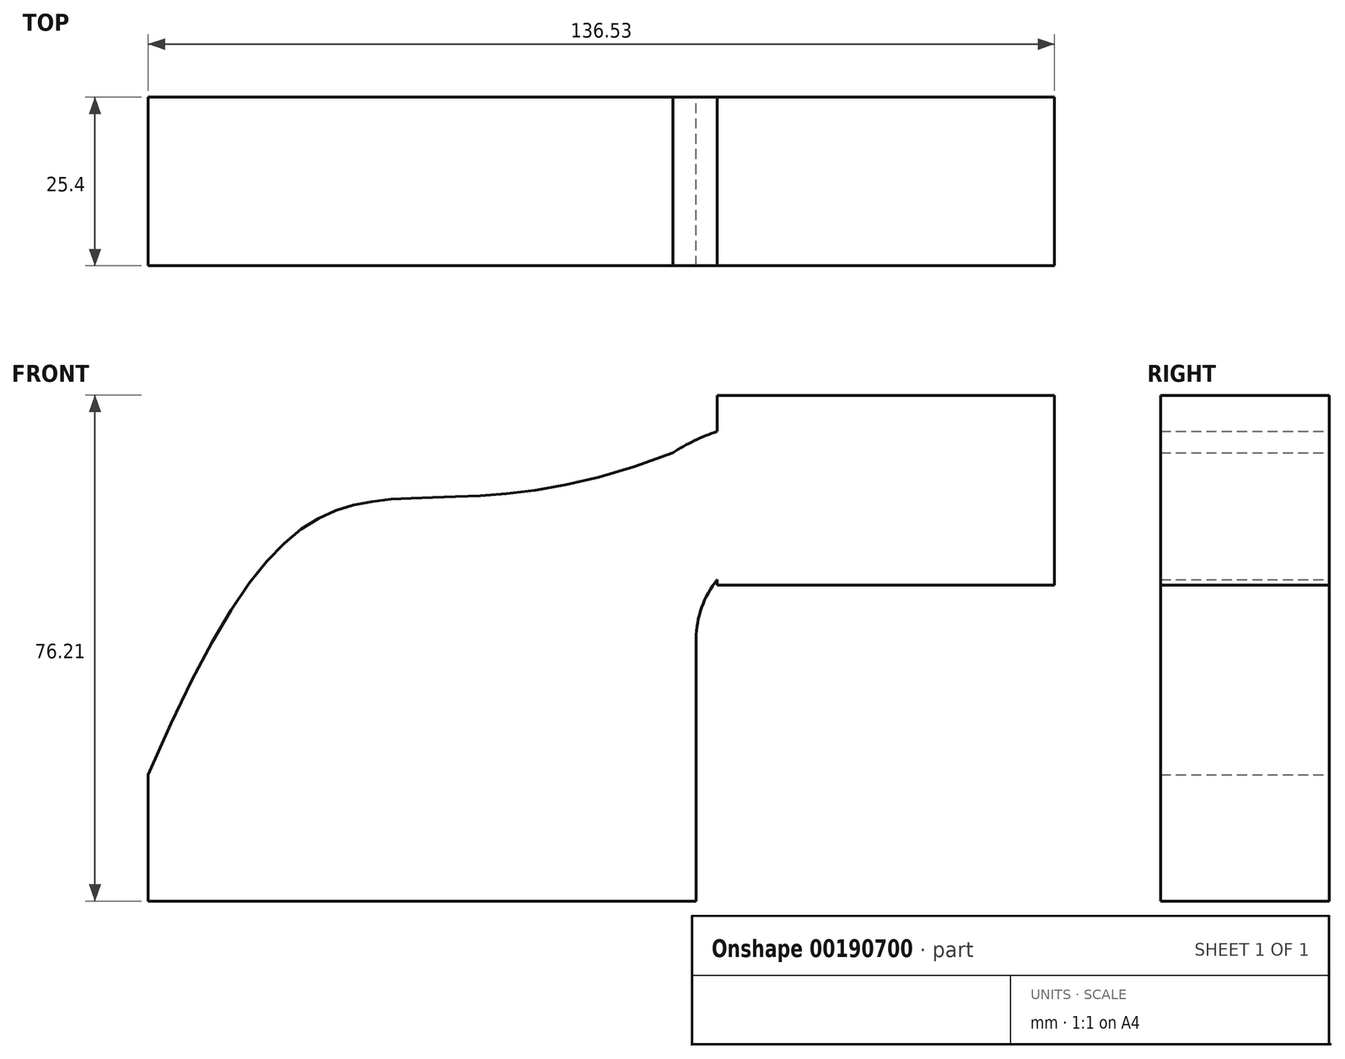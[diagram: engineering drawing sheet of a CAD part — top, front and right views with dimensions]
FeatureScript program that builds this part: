
annotation { "Feature Type Name" : "Feature", "Feature Type Description" : "" }
export const myFeature = defineFeature(function(context is Context, id is Id, definition is map)
    precondition{}
    {
        {
            var Q0;
            Q0=qCreatedBy(makeId("Front.planeOp"),FACE);
            var sketch = newSketch(context, id + "F0", { "sketchPlane" : qUnion([Q0])});
            skLineSegment(sketch, "E0.bottom", {"start": v(41.27, 9.53) * mm, "end": v(-41.28, 9.53) * mm});
            skLineSegment(sketch, "E0.top", {"start": v(41.28, -9.52) * mm, "end": v(-41.27, -9.52) * mm});
            skLineSegment(sketch, "E0.left", {"start": v(41.28, 9.53) * mm, "end": v(41.28, -9.52) * mm});
            skLineSegment(sketch, "E0.right", {"start": v(-41.28, 9.53) * mm, "end": v(-41.27, -9.52) * mm});
            skPoint(sketch, "E0.middle", {"position": v(0, 0) * mm});
            skLineSegment(sketch, "E1.bottom", {"start": v(95.25, 38.1) * mm, "end": v(44.45, 38.1) * mm});
            skLineSegment(sketch, "E1.top", {"start": v(95.25, 66.68) * mm, "end": v(44.45, 66.68) * mm});
            skLineSegment(sketch, "E1.left", {"start": v(95.25, 38.1) * mm, "end": v(95.25, 66.68) * mm});
            skLineSegment(sketch, "E1.right", {"start": v(44.45, 38.1) * mm, "end": v(44.45, 66.68) * mm});
            skPoint(sketch, "E1.middle", {"position": v(69.85, 52.39) * mm});
            skLineSegment(sketch, "E2", {"start": v(41.27, 9.53) * mm, "end": v(41.27, 30) * mm});
            skArc(sketch, "E3", {"start": v(41.27, 30) * mm, "mid": v(47.6, 41.72) * mm, "end": v(60.87, 42.88) * mm});
            skLineSegment(sketch, "E4", {"start": v(60.87, 42.88) * mm, "end": v(69.85, 42.88) * mm});
            skLineSegment(sketch, "E5.0", {"start": v(46.65, 61.93) * mm, "end": v(69.82, 61.93) * mm});
            skArc(sketch, "E5.1", {"start": v(22.22, 30) * mm, "mid": v(29.03, 50.1) * mm, "end": v(46.65, 61.93) * mm});
            skLineSegment(sketch, "E5.2", {"start": v(22.23, 9.53) * mm, "end": v(22.23, 30) * mm});
            skLineSegment(sketch, "E6", {"start": v(69.85, 66.68) * mm, "end": v(69.85, 38.1) * mm});
            skFitSpline(sketch, "E7", {"points": [v(-41.28, 9.53) * mm, v(46.65, 61.93) * mm], "startDerivative": vector(85.74, 198.9) * mm, "endDerivative": vector(163.47, 78.69) * mm});
            skSolve(sketch);
        }
        {
            var Q0;
            Q0 = qSketchRegion(id + "F0", true);
            extrude(context, id + "F1", {"entities" : qUnion([Q0]), "endBound" : BoundingType.SYMMETRIC, "depth" : 25.4 * mm});
        }
    });
